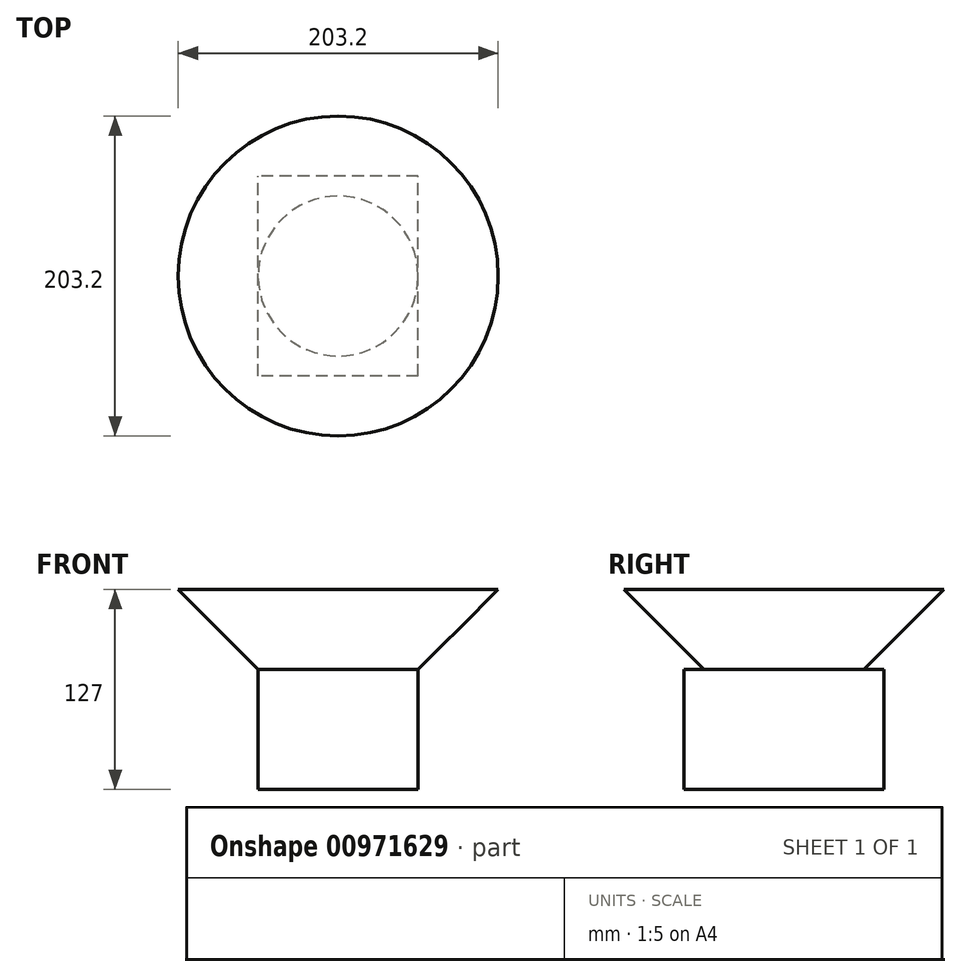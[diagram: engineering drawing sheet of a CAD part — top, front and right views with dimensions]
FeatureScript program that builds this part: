
annotation { "Feature Type Name" : "Feature", "Feature Type Description" : "" }
export const myFeature = defineFeature(function(context is Context, id is Id, definition is map)
    precondition{}
    {
        {
            var Q0;
            Q0=qCreatedBy(makeId("Front.planeOp"),FACE);
            var sketch = newSketch(context, id + "F0", { "sketchPlane" : qUnion([Q0])});
            skLineSegment(sketch, "E0.bottom", {"start": v(50.8, -38.1) * mm, "end": v(-50.8, -38.1) * mm});
            skLineSegment(sketch, "E0.top", {"start": v(50.8, 38.1) * mm, "end": v(-50.8, 38.1) * mm});
            skLineSegment(sketch, "E0.left", {"start": v(50.8, -38.1) * mm, "end": v(50.8, 38.1) * mm});
            skLineSegment(sketch, "E0.right", {"start": v(-50.8, -38.1) * mm, "end": v(-50.8, 38.1) * mm});
            skSolve(sketch);
        }
        {
            var Q0;
            Q0 = qSketchRegion(id + "F0", true);
            extrude(context, id + "F1", {"entities" : qUnion([Q0]), "depth" : 127 * mm, "offsetDistance" : 25.4 * mm});
        }
        {
            var Q0;
            Q0=makeQuery(id+"F1.opExtrude","SWEPT_FACE",FACE,{"disambiguationData":[OSD([sQuery(id+"F0.wireOp",EDGE,"E0.top")])]});
            var sketch = newSketch(context, id + "F2", { "sketchPlane" : qUnion([Q0])});
            skCircle(sketch, "E1", {"center": v(0, -63.5) * mm, "radius": 50.8 * mm});
            skPoint(sketch, "E2", {"position": v(50.8, -63.5) * mm});
            skSolve(sketch);
        }
        {
            var Q0;
            {var subQ0=sQuery(id+"F2.wireOp",EDGE,"E1");var subQ1=sQuery(id+"F0.wireOp",EDGE,"E0.top");var subQ2=makeQuery(id+"F2.imprint","INTERSECT",VERTEX,{"derivedFrom":[makeQuery(id+"F1.opExtrude","SWEPT_EDGE",EDGE,{"disambiguationData":[OSD([subQ1,sQuery(id+"F0.wireOp",EDGE,"E0.left")])]}),subQ0]});Q0=makeQuery(id+"F2.imprint","IMPRINT",FACE,{"disambiguationData":[TD([[makeQuery(id+"F2.imprint","IMPRINT",EDGE,{"disambiguationData":[TD([[subQ2,-1.0]])],"derivedFrom":subQ0}),1.0]])]});}
            extrude(context, id + "F3", {"entities" : qUnion([Q0]), "depth" : 50.8 * mm, "offsetDistance" : 25.4 * mm, "hasDraft" : true, "draftAngle" : 45 * degree});
        }
    });
